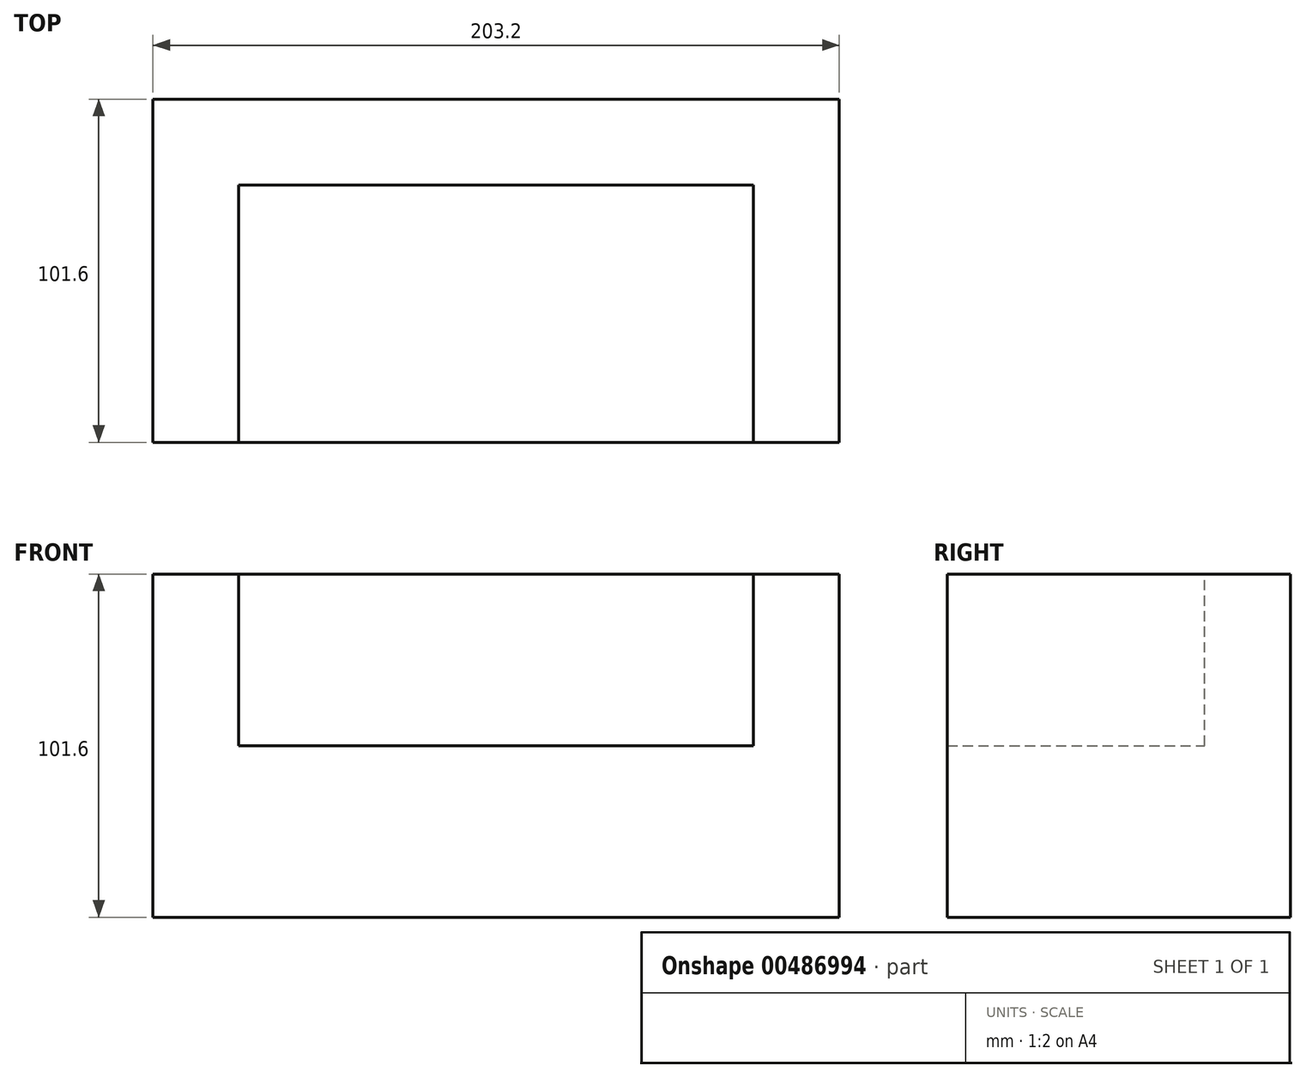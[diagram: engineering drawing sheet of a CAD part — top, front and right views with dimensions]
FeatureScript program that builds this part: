
annotation { "Feature Type Name" : "Feature", "Feature Type Description" : "" }
export const myFeature = defineFeature(function(context is Context, id is Id, definition is map)
    precondition{}
    {
        {
            var Q0;
            Q0=qCreatedBy(makeId("Front.planeOp"),FACE);
            var sketch = newSketch(context, id + "F0", { "sketchPlane" : qUnion([Q0])});
            skLineSegment(sketch, "E0.bottom", {"start": v(0, 0) * mm, "end": v(-203.2, 0) * mm});
            skLineSegment(sketch, "E0.top", {"start": v(-25.4, 50.8) * mm, "end": v(-177.8, 50.8) * mm});
            skLineSegment(sketch, "E0.left", {"start": v(0, 0) * mm, "end": v(0, 50.8) * mm});
            skLineSegment(sketch, "E0.right", {"start": v(-203.2, 0) * mm, "end": v(-203.2, 50.8) * mm});
            skLineSegment(sketch, "E1.top", {"start": v(0, 101.6) * mm, "end": v(-25.4, 101.6) * mm});
            skLineSegment(sketch, "E1.left", {"start": v(0, 50.8) * mm, "end": v(0, 101.6) * mm});
            skLineSegment(sketch, "E1.right", {"start": v(-25.4, 50.8) * mm, "end": v(-25.4, 101.6) * mm});
            skLineSegment(sketch, "E2.top", {"start": v(-203.2, 101.6) * mm, "end": v(-177.8, 101.6) * mm});
            skLineSegment(sketch, "E2.left", {"start": v(-203.2, 50.8) * mm, "end": v(-203.2, 101.6) * mm});
            skLineSegment(sketch, "E2.right", {"start": v(-177.8, 50.8) * mm, "end": v(-177.8, 101.6) * mm});
            skLineSegment(sketch, "E3.bottom", {"start": v(-177.8, 101.6) * mm, "end": v(-25.4, 101.6) * mm});
            skLineSegment(sketch, "E3.top", {"start": v(-177.8, 50.8) * mm, "end": v(-25.4, 50.8) * mm});
            skLineSegment(sketch, "E3.left", {"start": v(-177.8, 101.6) * mm, "end": v(-177.8, 50.8) * mm});
            skLineSegment(sketch, "E3.right", {"start": v(-25.4, 101.6) * mm, "end": v(-25.4, 50.8) * mm});
            skSolve(sketch);
        }
        {
            var Q0;
            Q0=makeQuery(id+"F0.imprint","IMPRINT",FACE,{"disambiguationData":[TD([[makeQuery(id+"F0.imprint","IMPRINT",EDGE,{"derivedFrom":sQuery(id+"F0.wireOp",EDGE,"E0.bottom")}),-1.0]])]});
            extrude(context, id + "F1", {"entities" : qUnion([Q0]), "depth" : 101.6 * mm});
        }
        {
            var Q0;
            Q0=makeQuery(id+"F0.imprint","IMPRINT",FACE,{"disambiguationData":[TD([[makeQuery(id+"F0.imprint","IMPRINT",EDGE,{"derivedFrom":sQuery(id+"F0.wireOp",EDGE,"E3.bottom")}),-1.0]])]});
            extrude(context, id + "F2", {"entities" : qUnion([Q0]), "operationType" : NewBodyOperationType.ADD, "depth" : 25.4 * mm});
        }
    });
